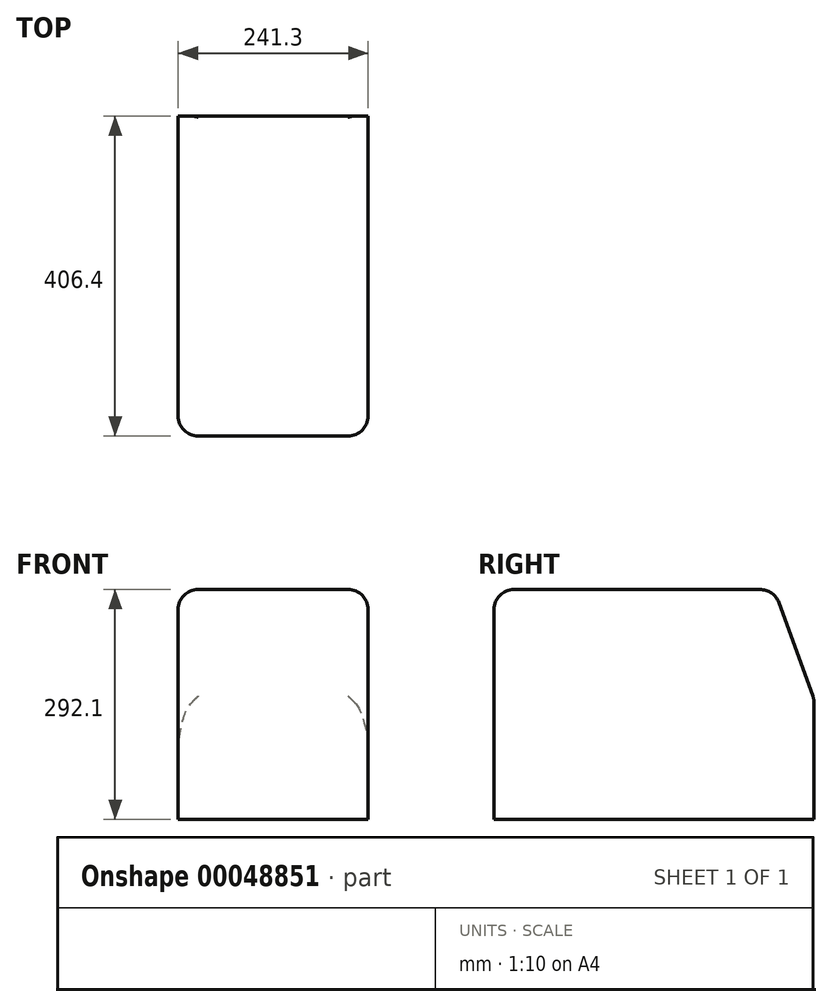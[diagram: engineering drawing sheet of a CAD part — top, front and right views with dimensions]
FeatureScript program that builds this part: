
annotation { "Feature Type Name" : "Feature", "Feature Type Description" : "" }
export const myFeature = defineFeature(function(context is Context, id is Id, definition is map)
    precondition{}
    {
        {
            var Q0;
            Q0=qCreatedBy(makeId("Right.planeOp"),FACE);
            var sketch = newSketch(context, id + "F0", { "sketchPlane" : qUnion([Q0])});
            skLineSegment(sketch, "E0.rect.bottom", {"start": v(152.4, 146.05) * mm, "end": v(-203.2, 146.05) * mm});
            skLineSegment(sketch, "E0.rect.top", {"start": v(203.2, -146.05) * mm, "end": v(-203.2, -146.05) * mm});
            skLineSegment(sketch, "E0.rect.left", {"start": v(203.2, 6.35) * mm, "end": v(203.2, -146.05) * mm});
            skLineSegment(sketch, "E0.rect.right", {"start": v(-203.2, 146.05) * mm, "end": v(-203.2, -146.05) * mm});
            skPoint(sketch, "E0.rect.middle", {"position": v(0, 0) * mm});
            skLineSegment(sketch, "E1", {"start": v(203.2, -146.05) * mm, "end": v(203.2, 6.35) * mm});
            skLineSegment(sketch, "E2", {"start": v(152.4, 146.05) * mm, "end": v(203.2, 6.35) * mm});
            skPoint(sketch, "E3.orphan", {"position": v(203.2, 146.05) * mm});
            skSolve(sketch);
        }
        {
            var Q0;
            Q0=makeQuery(id+"F0.imprint","IMPRINT",FACE,{"disambiguationData":[TD([[makeQuery(id+"F0.imprint","IMPRINT",EDGE,{"derivedFrom":sQuery(id+"F0.wireOp",EDGE,"E0.rect.bottom")}),1.0]])]});
            extrude(context, id + "F1", {"entities" : qUnion([Q0]), "depth" : 241.3 * mm});
        }
        {
            var Q0;
            Q0=makeQuery(id+"F1.opExtrude","CAP_EDGE",EDGE,{"disambiguationData":[OSD([sQuery(id+"F0.wireOp",EDGE,"E0.rect.bottom")])],"isStart":true});
            var Q1;
            Q1=makeQuery(id+"F1.opExtrude","SWEPT_EDGE",EDGE,{"disambiguationData":[OSD([sQuery(id+"F0.wireOp",EDGE,"E0.rect.bottom"),sQuery(id+"F0.wireOp",EDGE,"E0.rect.right")])]});
            var Q2;
            Q2=makeQuery(id+"F1.opExtrude","CAP_EDGE",EDGE,{"disambiguationData":[OSD([sQuery(id+"F0.wireOp",EDGE,"E0.rect.bottom")])],"isStart":false});
            var Q3;
            Q3=makeQuery(id+"F1.opExtrude","SWEPT_EDGE",EDGE,{"disambiguationData":[OSD([sQuery(id+"F0.wireOp",EDGE,"E0.rect.bottom"),sQuery(id+"F0.wireOp",EDGE,"E2")])]});
            var Q4;
            Q4=makeQuery(id+"F1.opExtrude","CAP_EDGE",EDGE,{"disambiguationData":[OSD([sQuery(id+"F0.wireOp",EDGE,"E2")])],"isStart":true});
            var Q5;
            Q5=makeQuery(id+"F1.opExtrude","CAP_EDGE",EDGE,{"disambiguationData":[OSD([sQuery(id+"F0.wireOp",EDGE,"E1")])],"isStart":true});
            var Q6;
            Q6=makeQuery(id+"F1.opExtrude","CAP_EDGE",EDGE,{"disambiguationData":[OSD([sQuery(id+"F0.wireOp",EDGE,"E0.rect.right")])],"isStart":true});
            var Q7;
            Q7=makeQuery(id+"F1.opExtrude","CAP_EDGE",EDGE,{"disambiguationData":[OSD([sQuery(id+"F0.wireOp",EDGE,"E0.rect.right")])],"isStart":false});
            var Q8;
            Q8=makeQuery(id+"F1.opExtrude","CAP_EDGE",EDGE,{"disambiguationData":[OSD([sQuery(id+"F0.wireOp",EDGE,"E2")])],"isStart":false});
            var Q9;
            Q9=makeQuery(id+"F1.opExtrude","CAP_EDGE",EDGE,{"disambiguationData":[OSD([sQuery(id+"F0.wireOp",EDGE,"E1")])],"isStart":false});
            var Q10;
            Q10=makeQuery(id+"F1.opExtrude","SWEPT_EDGE",EDGE,{"disambiguationData":[OSD([sQuery(id+"F0.wireOp",EDGE,"E1"),sQuery(id+"F0.wireOp",EDGE,"E2")])]});
            fillet(context, id + "F2", {"entities" : qUnion([Q0, Q1, Q2, Q3, Q4, Q5, Q6, Q7, Q8, Q9, Q10]), "radius" : 25.4 * mm, "tangentPropagation" : true, "allowEdgeOverflow" : false});
        }
    });
